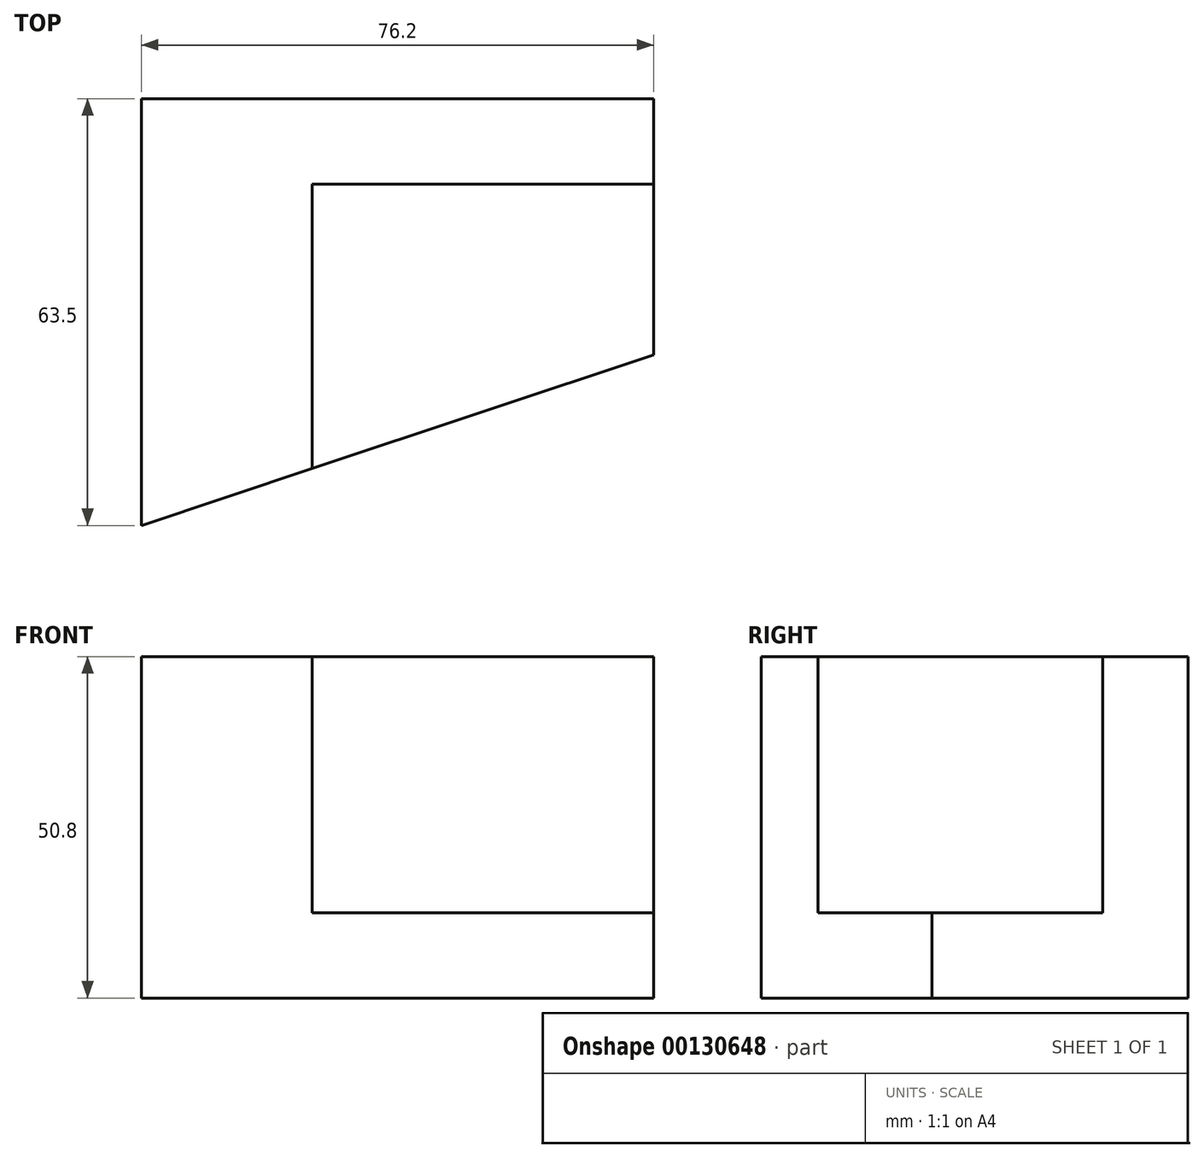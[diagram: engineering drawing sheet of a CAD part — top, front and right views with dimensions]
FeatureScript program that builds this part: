
annotation { "Feature Type Name" : "Feature", "Feature Type Description" : "" }
export const myFeature = defineFeature(function(context is Context, id is Id, definition is map)
    precondition{}
    {
        {
            var Q0;
            Q0=qCreatedBy(makeId("Front.planeOp"),FACE);
            var sketch = newSketch(context, id + "F0", { "sketchPlane" : qUnion([Q0])});
            skLineSegment(sketch, "E0", {"start": v(0, 0) * mm, "end": v(76.2, 0) * mm});
            skLineSegment(sketch, "E1", {"start": v(76.2, 0) * mm, "end": v(76.2, 50.8) * mm});
            skLineSegment(sketch, "E2", {"start": v(76.2, 50.8) * mm, "end": v(0, 50.8) * mm});
            skLineSegment(sketch, "E3", {"start": v(25.4, 50.8) * mm, "end": v(25.4, 12.7) * mm});
            skLineSegment(sketch, "E4", {"start": v(25.4, 12.7) * mm, "end": v(76.2, 12.7) * mm});
            skLineSegment(sketch, "E5", {"start": v(0, 0) * mm, "end": v(0, 50.8) * mm});
            skSolve(sketch);
        }
        {
            var Q0;
            {var subQ4=sQuery(id+"F0.wireOp",EDGE,"E0");Q0=makeQuery(id+"F0.imprint","IMPRINT",FACE,{"disambiguationData":[TD([[makeQuery(id+"F0.imprint","IMPRINT",EDGE,{"derivedFrom":subQ4}),1.0]])]});}
            extrude(context, id + "F1", {"entities" : qUnion([Q0]), "endBound" : BoundingType.SYMMETRIC, "depth" : 63.5 * mm});
        }
        {
            var Q0;
            Q0=makeQuery(id+"F1.opExtrude","SWEPT_FACE",FACE,{"disambiguationData":[OSD([sQuery(id+"F0.wireOp",EDGE,"E4")])]});
            var sketch = newSketch(context, id + "F2", { "sketchPlane" : qUnion([Q0])});
            skLineSegment(sketch, "E6", {"start": v(25.4, 31.75) * mm, "end": v(76.2, 31.75) * mm});
            skLineSegment(sketch, "E7", {"start": v(76.2, 31.75) * mm, "end": v(76.2, 19.05) * mm});
            skLineSegment(sketch, "E8", {"start": v(76.2, 19.05) * mm, "end": v(25.4, 19.05) * mm});
            skLineSegment(sketch, "E9", {"start": v(25.4, 19.05) * mm, "end": v(25.4, 31.75) * mm});
            skSolve(sketch);
        }
        {
            var Q0;
            Q0 = qSketchRegion(id + "F2", true);
            extrude(context, id + "F3", {"entities" : qUnion([Q0]), "operationType" : NewBodyOperationType.ADD, "depth" : 38.1 * mm});
        }
        {
            var Q0;
            Q0=qCreatedBy(makeId("Top.planeOp"),FACE);
            var sketch = newSketch(context, id + "F4", { "sketchPlane" : qUnion([Q0])});
            skLineSegment(sketch, "E10", {"start": v(0, -31.75) * mm, "end": v(76.2, -6.35) * mm});
            skLineSegment(sketch, "E11", {"start": v(76.2, -6.35) * mm, "end": v(76.2, -31.75) * mm});
            skLineSegment(sketch, "E12", {"start": v(76.2, -31.75) * mm, "end": v(0, -31.75) * mm});
            skSolve(sketch);
        }
        {
            var Q0;
            Q0 = qSketchRegion(id + "F4", true);
            extrude(context, id + "F5", {"entities" : qUnion([Q0]), "operationType" : NewBodyOperationType.REMOVE, "endBound" : BoundingType.THROUGH_ALL, "depth" : 25.4 * mm});
        }
    });
